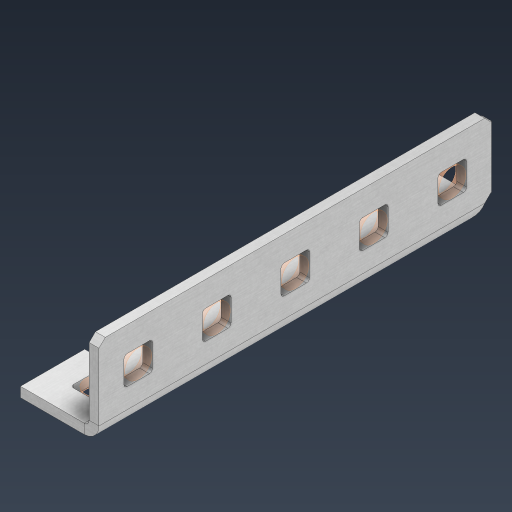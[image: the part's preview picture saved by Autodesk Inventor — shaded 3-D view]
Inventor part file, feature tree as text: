
AUTODESK INVENTOR PART (.ipt)
format: ipt  version: 2024.3 (Build 283343000, 343)  size: 492,032 bytes
history: native  units: in
note: dims shown in document units (in); Inventor stores cm internally (conversion verified against a paired STEP export)
features: other x22, extrude x13, sheet_metal_op x11, pattern_linear x2, mirror x1, chamfer x1, sketch x1
ambient origin geometry x8: Origin, YZ Plane, XZ Plane, XY Plane, X Axis, Y Axis, Z Axis, Center Point
bodies: Solid1 (feature_tree), Body (feature_tree)
feature tree (51):
  sheet_metal_op  "Flanges"
  other  "Flange Pattern Plane"
  other  "Flange Pattern Sketch"
  sheet_metal_op  "Flange Pattern"
  sheet_metal_op  "Body Pattern"
  pattern_linear  "Center Pattern"  Spacing1=2.5in  [1 undecoded]
  other  "Arc Length"
  mirror  "Notch Mirror"
  pattern_linear  "Notch Pattern"  Spacing1=0.0625in  [1 undecoded]
  chamfer  "End Chamfer"
  extrude  "Half Cut"  Depth=0.0625in
  other  "Plate1"
  sketch  "Sketch2"  dims[d0=1.0in d1=2.5in d2=0.0625in d3=0.0625in d4=0.0312in d5=0.125in d6=0.0625in d7=0.5in d8=90.0deg d9=0.0312in d10=0.25in d11=0.0625in d12=0.0625in d16=0.182in d17=0.02in d18=0.0625in d19=0.0in d20=0.25in d21=0.25in d38=1.9685in d40=0.5in d41=0.3937in d43=1.0in d46=0.172in d47=1.0in d48=0.0in d49=0.182in d50=0.02in d51=0.25in d52=0.25in d53=0.0625in d54=0.0in d55=0.172in d56=1.0in d57=0.0in d58=0.25in d60=1.9685in d62=0.5in d63=0.3937in d65=0.5in d85=0.1473in d86=0.1782in d88=0.04in d89=0.0625in d90=0.0in d91=0.04in d92=0.0491in d95=2.5in d96=0.04in d97=0.25in d98=45.0deg d99=0.25in d100=0.5in d101=0.0in d102=2.497in d106=0.182in d107=0.02in d108=0.5in d109=0.5in d110=0.0625in d111=0.0in d112=0.172in d113=0.5in d114=0.0in d117=0.5in d118=0.5in d119=0.5in]
  other  "Plate2"
  sheet_metal_op  "Bend1"
  sheet_metal_op  "Corner1"
  other  "Srf1"
  other  "Srf2"
  other  "Srf91"
  sheet_metal_op  "Body Pattern Sketch"
  other  "Srf92"
  other  "Srf786"
  other  "Srf823"
  other  "Srf824"
  other  "Srf825"
  other  "Srf856"
  other  "Srf857"
  other  "Srf858"
  other  "Srf889"
  other  "Srf890"
  other  "Srf891"
  other  "Srf892"
  sheet_metal_op  "Flange Stamp"
  sheet_metal_op  "Flange Circle"
  sheet_metal_op  "Body Stamp"
  sheet_metal_op  "Body Circle"
  other  "Center Stamp"
  other  "Center Circle"
  sheet_metal_op  "Notch"
  extrude  "ExtrusionSrf2"  Depth=0.5in
  extrude  "ExtrusionSrf92"  Depth=0.5in
  extrude  "ExtrusionSrf823"  Depth=0.0625in
  extrude  "ExtrusionSrf824"  Depth=0.5in TaperAngle=90.0deg
  extrude  "ExtrusionSrf825"  Depth=0.5in
  extrude  "ExtrusionSrf856"  Depth=0.0625in
  extrude  "ExtrusionSrf857"  Depth=0.0625in
  extrude  "ExtrusionSrf858"  Depth=0.182in
  extrude  "ExtrusionSrf889"  Depth=0.02in
  extrude  "ExtrusionSrf890"  Depth=0.0625in
  extrude  "ExtrusionSrf891"  TaperAngle=0.0deg  [1 undecoded]
  extrude  "ExtrusionSrf892"  Depth=0.5in
note: 3 required parameter values undecoded (feature->parameter linkage not recoverable at this tier; creation-order binding heuristic only, values carry confidence <= 0.55)
